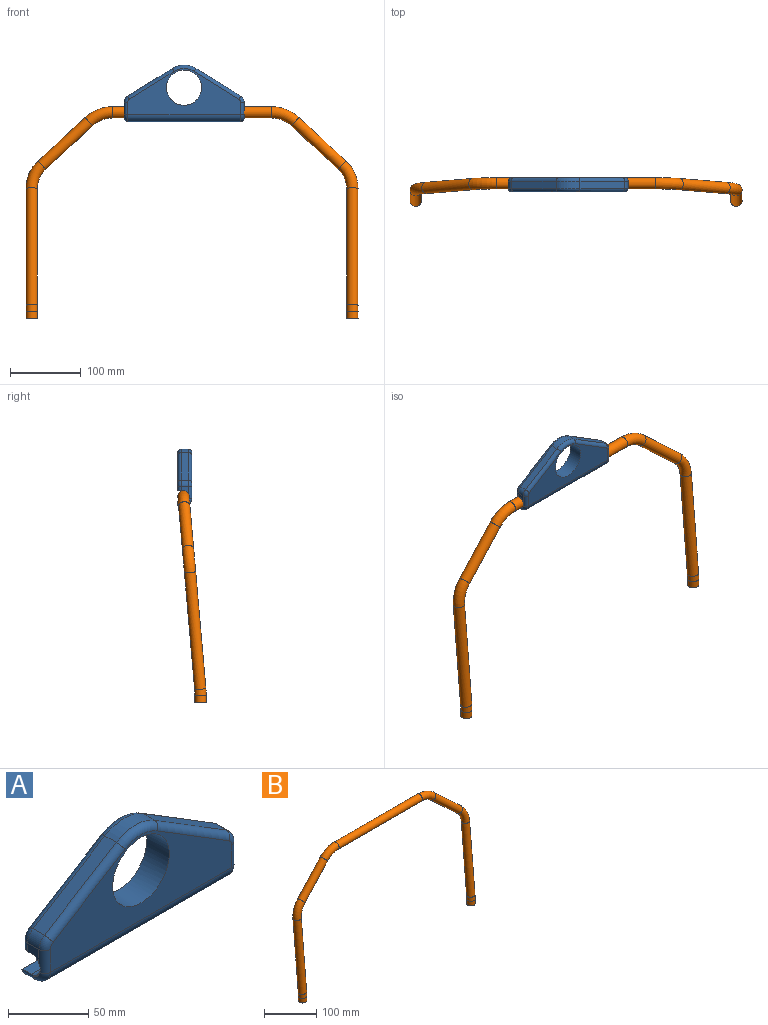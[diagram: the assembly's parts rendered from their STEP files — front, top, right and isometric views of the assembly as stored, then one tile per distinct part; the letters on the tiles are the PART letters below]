
ASSEMBLY  parts=2 mates=1
PART A: 36 faces, bbox 171.6x20.8x83.5 mm
  f0: plane 6.88x3.92mm, normal (-1,0,0), area 3mm2, adj f10,f18,f19
  f1: plane 6.88x3.92mm, normal (1,0,0), area 3mm2, adj f10,f27,f28
  f2: plane 10.56x10mm, normal (-1,0,0), area 72.7mm2, adj f9,f10,f16,f20,f29
  f3: plane 160x65mm, normal (0,-1,0), area 5184.7mm2, adj f11,f15,f20,f21,f22,f23,f24,f25
  f4: plane 10.56x10mm, normal (1,0,0), area 72.7mm2, adj f9,f10,f17,f26,f35
  f5: plane 160x54mm, normal (0,1,0), area 3424.7mm2, adj f9,f11,f29,f30,f31,f32,f33,f34
  f6: plane 160x10mm, normal (0,0,-1), area 1600mm2, adj f7,f15,f18,f28
  f7: plane 170x5mm, normal (0,1,0), area 839.3mm2, adj f6,f8,f18,f28
  f8: plane 170x8mm, normal (0,0,1), area 1360mm2, adj f7,f10,f18,f28
  f9: plane 170x8mm, normal (0,0,-1), area 1349.3mm2, adj f2,f4,f5,f10,f29,f35
  f10: cylinder r=8mm len=170mm, axis (1,0,0), area 4272.4mm2, adj f0,f1,f2,f4,f8,f9,f19,f20
  f11: cylinder r=25mm len=50mm, axis (0,1,0), area 3141.6mm2, adj f3,f5
  f12: plane 63.42x39.27mm, normal (0.53,0,0.85), area 745.9mm2, adj f13,f17,f24,f33
  f13: cylinder r=32mm len=33.7mm, axis (0,1,0), area 354.9mm2, adj f12,f14,f23,f32
  f14: plane 63.42x39.27mm, normal (-0.53,0,0.85), area 745.9mm2, adj f13,f16,f22,f31
  f15: cylinder r=10mm len=160mm, axis (-1,0,0), area 2513.3mm2, adj f3,f6,f19,f27
  f16: cylinder r=10mm len=10mm, axis (0,1,0), area 101.6mm2, adj f2,f14,f21,f30
  f17: cylinder r=10mm len=10mm, axis (0,1,0), area 101.6mm2, adj f4,f12,f25,f34
  f18: cylinder r=5mm len=10mm, axis (0,1,0), area 78.5mm2, adj f0,f6,f7,f8,f19
  f19: torus R=5mm, axis (-1,0,0), area 100.7mm2, adj f0,f10,f15,f18,f20
  f20: cylinder r=5mm len=17.43mm, axis (0,0,1), area 131.8mm2, adj f2,f3,f10,f19,f21
  f21: torus R=5mm, axis (0,-1,0), area 65.3mm2, adj f3,f16,f20,f22
  f22: cylinder r=5mm len=66.05mm, axis (-0.85,0,-0.53), area 585.9mm2, adj f3,f14,f21,f23
  f23: torus R=27mm, axis (0,-1,0), area 262.9mm2, adj f3,f13,f22,f24
  f24: cylinder r=5mm len=66.05mm, axis (-0.85,0,0.53), area 585.9mm2, adj f3,f12,f23,f25
  f25: torus R=5mm, axis (0,-1,0), area 65.3mm2, adj f3,f17,f24,f26
  f26: cylinder r=5mm len=17.43mm, axis (0,0,-1), area 131.8mm2, adj f3,f4,f10,f25,f27
  f27: torus R=5mm, axis (-1,0,0), area 100.7mm2, adj f1,f10,f15,f26,f28
  f28: cylinder r=5mm len=10mm, axis (0,-1,0), area 78.5mm2, adj f1,f6,f7,f8,f27
  f29: cylinder r=5mm len=6.43mm, axis (0,0,-1), area 50.5mm2, adj f2,f5,f9,f30
  f30: torus R=5mm, axis (0,-1,0), area 65.3mm2, adj f5,f16,f29,f31
  f31: cylinder r=5mm len=66.05mm, axis (-0.85,0,-0.53), area 585.9mm2, adj f5,f14,f30,f32
  f32: torus R=27mm, axis (0,-1,0), area 262.9mm2, adj f5,f13,f31,f33
  f33: cylinder r=5mm len=66.05mm, axis (-0.85,0,0.53), area 585.9mm2, adj f5,f12,f32,f34
  f34: torus R=5mm, axis (0,-1,0), area 65.3mm2, adj f5,f17,f33,f35
  f35: cylinder r=5mm len=6.43mm, axis (0,0,1), area 50.5mm2, adj f4,f5,f9,f34
PART B: 28 faces, bbox 479.6x40.4x305.6 mm
  f0: cylinder r=6mm len=12mm, axis (0,0,1), area 400.9mm2, adj f1,f3
  f1: torus R=100mm, axis (-1,0,0), area 329mm2, adj f0,f2
  f2: cylinder r=6mm len=166.68mm, axis (0,0.09,1), area 6268mm2, adj f1,f7
  f3: plane 16x16mm, normal (0,0,-1), area 88mm2, adj f0,f4
  f4: cylinder r=8mm len=16mm, axis (0,0,1), area 534.5mm2, adj f3,f5
  f5: torus R=100mm, axis (-1,0,0), area 438.6mm2, adj f4,f6
  f6: cylinder r=8mm len=167.03mm, axis (0,0.09,1), area 8357.3mm2, adj f5,f11
  f7: torus R=45mm, axis (0,1,-0.09), area 1392.2mm2, adj f2,f8
  f8: cylinder r=6mm len=74.63mm, axis (0.73,0.06,0.68), area 3424mm2, adj f7,f9
  f9: torus R=50mm, axis (0,1,-0.09), area 1414mm2, adj f8,f10
  f10: cylinder r=6mm len=225.12mm, axis (1,0,0), area 8486.8mm2, adj f9,f24
  f11: torus R=45mm, axis (0,1,-0.09), area 1856.3mm2, adj f6,f12
  f12: cylinder r=8mm len=77.35mm, axis (0.73,0.06,0.68), area 4565.3mm2, adj f11,f13
  f13: torus R=50mm, axis (0,1,-0.09), area 1885.3mm2, adj f12,f14
  f14: cylinder r=8mm len=225.12mm, axis (1,0,0), area 11315.8mm2, adj f13,f27
  f15: cylinder r=6mm len=12mm, axis (0,0,1), area 400.9mm2, adj f16,f18
  f16: torus R=100mm, axis (1,0,0), area 329mm2, adj f15,f17
  f17: cylinder r=6mm len=166.68mm, axis (0,0.09,1), area 6268mm2, adj f16,f22
  f18: plane 16x16mm, normal (0,0,-1), area 88mm2, adj f15,f19
  f19: cylinder r=8mm len=16mm, axis (0,0,1), area 534.5mm2, adj f18,f20
  f20: torus R=100mm, axis (1,0,0), area 438.6mm2, adj f19,f21
  f21: cylinder r=8mm len=167.03mm, axis (0,0.09,1), area 8357.3mm2, adj f20,f25
  f22: torus R=45mm, axis (0,1,-0.09), area 1392.2mm2, adj f17,f23
  f23: cylinder r=6mm len=74.63mm, axis (-0.73,0.06,0.68), area 3424mm2, adj f22,f24
  f24: torus R=50mm, axis (0,1,-0.09), area 1414mm2, adj f10,f23
  f25: torus R=45mm, axis (0,1,-0.09), area 1856.3mm2, adj f21,f26
  f26: cylinder r=8mm len=77.35mm, axis (-0.73,0.06,0.68), area 4565.3mm2, adj f25,f27
  f27: torus R=50mm, axis (0,1,-0.09), area 1885.3mm2, adj f14,f26
PLACE A t=(216.22,32.31,319.83)mm
PLACE B at identity fixed
MATE slider A.f10 <-> B.f10  axis (1,0,0) through (216.22,24.31,292.83)mm
